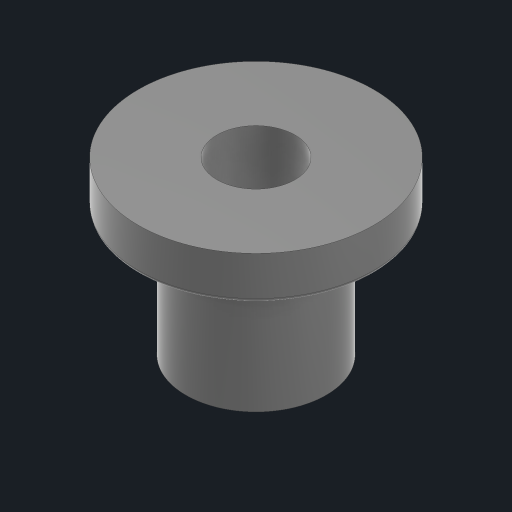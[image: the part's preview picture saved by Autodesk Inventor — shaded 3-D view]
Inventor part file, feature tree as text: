
AUTODESK INVENTOR PART (.ipt)
format: ipt  version: 2023 (Build 270158030, 158C)  size: 365,056 bytes
history: native  units: in
note: dims shown in document units (in); Inventor stores cm internally (conversion verified against a paired STEP export)
features: fillet x1
ambient origin geometry x8: Origin, YZ Plane, XZ Plane, XY Plane, X Axis, Y Axis, Z Axis, Center Point
bodies: Solid1 (feature_tree)
feature tree (1):
  fillet  "Fillet3"  [1 undecoded]
note: 1 required parameter value undecoded (feature->parameter linkage not recoverable at this tier; creation-order binding heuristic only, values carry confidence <= 0.55)
